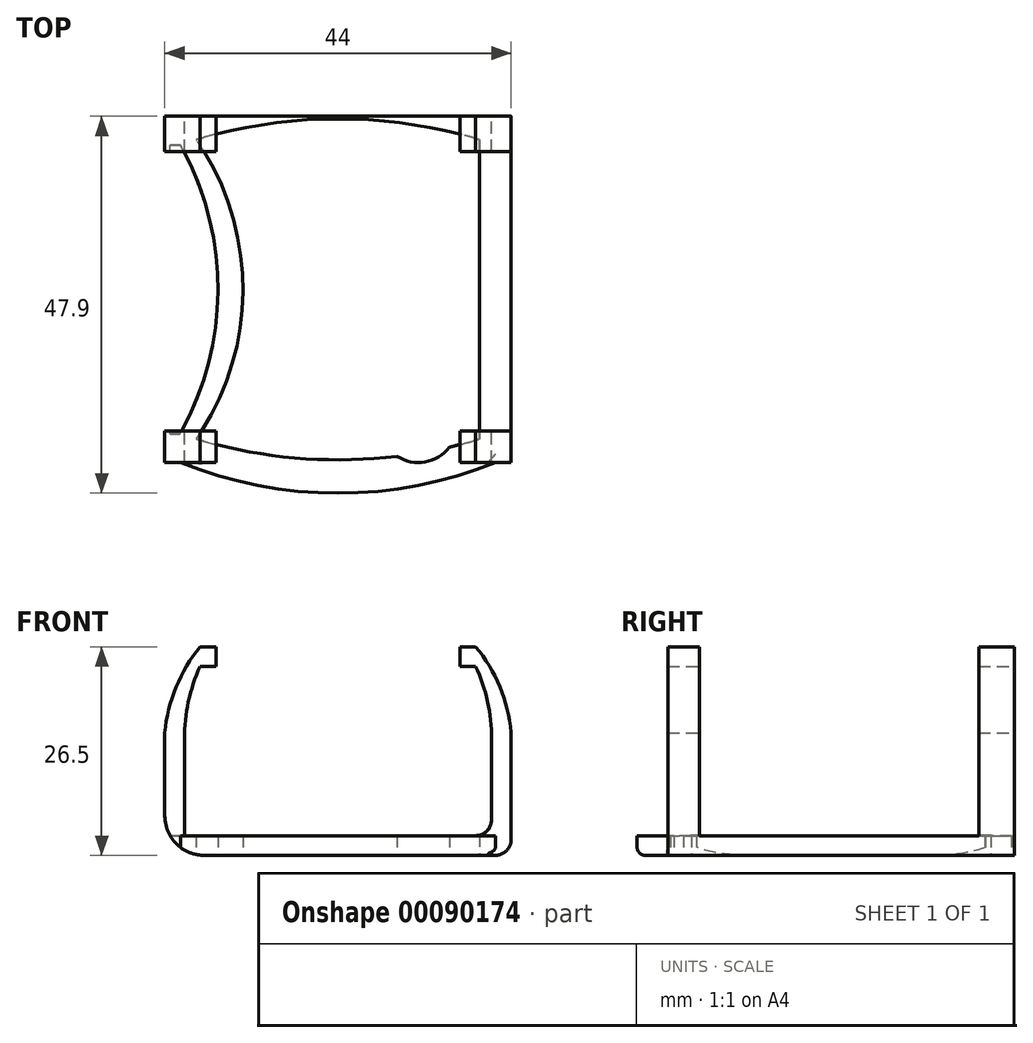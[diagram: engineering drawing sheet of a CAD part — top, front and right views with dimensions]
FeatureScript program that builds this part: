
annotation { "Feature Type Name" : "Feature", "Feature Type Description" : "" }
export const myFeature = defineFeature(function(context is Context, id is Id, definition is map)
    precondition{}
    {
        {
            var Q0;
            Q0=qCreatedBy(makeId("Front.planeOp"),FACE);
            var sketch = newSketch(context, id + "F0", { "sketchPlane" : qUnion([Q0])});
            skLineSegment(sketch, "E0", {"start": v(0, 0) * mm, "end": v(19.5, 0) * mm});
            skLineSegment(sketch, "E1", {"start": v(19.5, 0) * mm, "end": v(19.5, 12.3) * mm});
            skLineSegment(sketch, "E2", {"start": v(22, 13.05) * mm, "end": v(22, -2.5) * mm});
            skLineSegment(sketch, "E3", {"start": v(22, -2.5) * mm, "end": v(0, -2.5) * mm});
            skArc(sketch, "E4", {"start": v(19.5, 12.3) * mm, "mid": v(19.01, 17.02) * mm, "end": v(17.5, 21.5) * mm});
            skArc(sketch, "E5", {"start": v(22, 13.05) * mm, "mid": v(20.57, 18.86) * mm, "end": v(17.5, 24) * mm});
            skLineSegment(sketch, "E6", {"start": v(17.5, 21.5) * mm, "end": v(15.5, 21.5) * mm});
            skLineSegment(sketch, "E7", {"start": v(15.5, 21.5) * mm, "end": v(15.5, 24) * mm});
            skLineSegment(sketch, "E8", {"start": v(15.5, 24) * mm, "end": v(17.5, 24) * mm});
            skLineSegment(sketch, "E9.MirrorCS", {"start": v(-17.5, 21.5) * mm, "end": v(-15.5, 21.5) * mm});
            skArc(sketch, "E10.MirrorCS", {"start": v(-19.5, 12.3) * mm, "mid": v(-19.01, 17.02) * mm, "end": v(-17.5, 21.5) * mm});
            skLineSegment(sketch, "E11.MirrorCS", {"start": v(-22, 13.05) * mm, "end": v(-22, -2.5) * mm});
            skLineSegment(sketch, "E12.MirrorCS", {"start": v(-19.5, 0) * mm, "end": v(-19.5, 12.3) * mm});
            skArc(sketch, "E13.MirrorCS", {"start": v(-22, 13.05) * mm, "mid": v(-20.57, 18.86) * mm, "end": v(-17.5, 24) * mm});
            skLineSegment(sketch, "E14.MirrorCS", {"start": v(-15.5, 24) * mm, "end": v(-17.5, 24) * mm});
            skLineSegment(sketch, "E15.MirrorCS", {"start": v(-22, -2.5) * mm, "end": v(0, -2.5) * mm});
            skLineSegment(sketch, "E16.MirrorCS", {"start": v(0, 0) * mm, "end": v(-19.5, 0) * mm});
            skLineSegment(sketch, "E17.MirrorCS", {"start": v(-15.5, 21.5) * mm, "end": v(-15.5, 24) * mm});
            skSolve(sketch);
        }
        {
            var Q0;
            Q0=makeQuery(id+"F0.imprint","IMPRINT",FACE,{"disambiguationData":[TD([[makeQuery(id+"F0.imprint","IMPRINT",EDGE,{"derivedFrom":sQuery(id+"F0.wireOp",EDGE,"E0")}),-1.0]])]});
            extrude(context, id + "F1", {"entities" : qUnion([Q0]), "depth" : 44 * mm});
        }
        {
            var Q0;
            Q0=makeQuery(id+"F1.opExtrude","SWEPT_FACE",FACE,{"disambiguationData":[OSD([sQuery(id+"F0.wireOp",EDGE,"E2")])]});
            var sketch = newSketch(context, id + "F2", { "sketchPlane" : qUnion([Q0])});
            skLineSegment(sketch, "E18", {"start": v(-40, 13.05) * mm, "end": v(-40, 0) * mm});
            skLineSegment(sketch, "E19", {"start": v(-40, 0) * mm, "end": v(-4.5, 0) * mm});
            skLineSegment(sketch, "E20", {"start": v(-4.5, 0) * mm, "end": v(-4.5, 13.05) * mm});
            skLineSegment(sketch, "E21", {"start": v(-4.5, 13.05) * mm, "end": v(-4.5, 24.05) * mm});
            skLineSegment(sketch, "E22", {"start": v(-4.5, 24.05) * mm, "end": v(-40, 24.05) * mm});
            skLineSegment(sketch, "E23", {"start": v(-40, 24.05) * mm, "end": v(-40, 13.05) * mm});
            skSolve(sketch);
        }
        {
            var Q0;
            Q0=makeQuery(id+"F1.opExtrude","SWEPT_EDGE",EDGE,{"disambiguationData":[OSD([sQuery(id+"F0.wireOp",EDGE,"ead0873c-5f46-45a2-a165-93b22b89707c5.MirrorCS"),sQuery(id+"F0.wireOp",EDGE,"ead0873c-5f46-45a2-a165-93b22b89707c6.MirrorCS")])]});
            var Q1;
            Q1=makeQuery(id+"F1.opExtrude","SWEPT_EDGE",EDGE,{"disambiguationData":[OSD([sQuery(id+"F0.wireOp",EDGE,"Wcccyxxx-FNSd-Qq9p-4Mge-pHL6YJXQHdxu"),sQuery(id+"F0.wireOp",EDGE,"E2")])]});
            var Q2;
            Q2=makeQuery(id+"F1.opExtrude","SWEPT_EDGE",EDGE,{"disambiguationData":[OSD([sQuery(id+"F0.wireOp",EDGE,"ead0873c-5f46-45a2-a165-93b22b89707c2.MirrorCS"),sQuery(id+"F0.wireOp",EDGE,"ead0873c-5f46-45a2-a165-93b22b89707c3.MirrorCS")])]});
            var Q3;
            Q3=makeQuery(id+"F1.opExtrude","SWEPT_EDGE",EDGE,{"disambiguationData":[OSD([sQuery(id+"F0.wireOp",EDGE,"E0"),sQuery(id+"F0.wireOp",EDGE,"E1")])]});
            var Q4;
            Q4=makeQuery(id+"F1.opExtrude","SWEPT_EDGE",EDGE,{"disambiguationData":[OSD([sQuery(id+"F0.wireOp",EDGE,"ead0873c-5f46-45a2-a165-93b22b89707c4.MirrorCS"),sQuery(id+"F0.wireOp",EDGE,"ead0873c-5f46-45a2-a165-93b22b89707c5.MirrorCS")])]});
            var Q5;
            Q5=makeQuery(id+"F1.opExtrude","SWEPT_EDGE",EDGE,{"disambiguationData":[OSD([sQuery(id+"F0.wireOp",EDGE,"E2"),sQuery(id+"F0.wireOp",EDGE,"E3")])]});
            fillet(context, id + "F3", {"entities" : qUnion([Q0, Q1, Q2, Q3, Q4, Q5]), "radius" : 2 * mm, "tangentPropagation" : true, "allowEdgeOverflow" : false});
        }
        {
            var Q0;
            Q0 = qSketchRegion(id + "F2", true);
            extrude(context, id + "F4", {"entities" : qUnion([Q0]), "operationType" : NewBodyOperationType.REMOVE, "endBound" : BoundingType.THROUGH_ALL, "oppositeDirection" : true, "depth" : 25 * mm});
        }
        {
            var Q0;
            Q0=makeQuery(id+"F1.opExtrude","SWEPT_FACE",FACE,{"disambiguationData":[OSD([sQuery(id+"F0.wireOp",EDGE,"E3"),sQuery(id+"F0.wireOp",EDGE,"ead0873c-5f46-45a2-a165-93b22b89707c4.MirrorCS")])]});
            var sketch = newSketch(context, id + "F5", { "sketchPlane" : qUnion([Q0])});
            skArc(sketch, "E24", {"start": v(20, 44) * mm, "mid": v(0, 47.9) * mm, "end": v(-20, 44) * mm});
            skArc(sketch, "E25", {"start": v(14.17, 42.04) * mm, "mid": v(11.06, 43.92) * mm, "end": v(7.5, 43.2) * mm});
            skLineSegment(sketch, "E26", {"start": v(-25.94, 40.39) * mm, "end": v(33.24, 40.39) * mm, "construction": true});
            skArc(sketch, "E27", {"start": v(18, 41.02) * mm, "mid": v(16.1, 41.56) * mm, "end": v(14.17, 42.04) * mm});
            skLineSegment(sketch, "E28", {"start": v(20, 22) * mm, "end": v(-23.8, 22) * mm, "construction": true});
            skArc(sketch, "E29.MirrorCS", {"start": v(18, 2.98) * mm, "mid": v(0, 0.34) * mm, "end": v(-18, 2.98) * mm});
            skArc(sketch, "E30.MirrorCS", {"start": v(20, 0) * mm, "mid": v(0, -3.9) * mm, "end": v(-20, 0) * mm});
            skArc(sketch, "E31.trimOffspring", {"start": v(7.5, 43.2) * mm, "mid": v(-5.36, 43.43) * mm, "end": v(-18, 41.02) * mm});
            skLineSegment(sketch, "E32", {"start": v(18, 47.5) * mm, "end": v(18, 44.76) * mm});
            skLineSegment(sketch, "E33.MirrorCS", {"start": v(-18, 41.02) * mm, "end": v(-18, 40.39) * mm});
            skPoint(sketch, "E34.orphan", {"position": v(-18, 47.5) * mm});
            skPoint(sketch, "E35.orphan", {"position": v(-20, 40.39) * mm});
            skPoint(sketch, "E36.orphan", {"position": v(-20, 3.61) * mm});
            skPoint(sketch, "E37.orphan", {"position": v(-18, -5.06) * mm});
            skPoint(sketch, "E38.trimOffspring.end.orphan", {"position": v(18, -5.06) * mm});
            skPoint(sketch, "E39.orphan", {"position": v(20, 3.61) * mm});
            skPoint(sketch, "E40.orphan", {"position": v(20, 40.39) * mm});
            skLineSegment(sketch, "E41.trimOffspring", {"start": v(18, 41.02) * mm, "end": v(18, 2.98) * mm});
            skLineSegment(sketch, "E42", {"start": v(-20, 44) * mm, "end": v(-20, 40.39) * mm});
            skLineSegment(sketch, "E43", {"start": v(20, 44) * mm, "end": v(20, 0) * mm});
            skArc(sketch, "E44", {"start": v(-18, 2.98) * mm, "mid": v(-12.07, 22) * mm, "end": v(-18, 41.02) * mm});
            skArc(sketch, "E45", {"start": v(-20, 3.61) * mm, "mid": v(-15.24, 22) * mm, "end": v(-20, 40.39) * mm});
            skLineSegment(sketch, "E46.trimOffspring", {"start": v(-20, 3.61) * mm, "end": v(-20, 0) * mm});
            skSolve(sketch);
        }
        {
            var Q0;
            {var subQ5=sQuery(id+"F5.wireOp",EDGE,"E27");Q0=makeQuery(id+"F5.imprint","IMPRINT",FACE,{"disambiguationData":[TD([[makeQuery(id+"F5.imprint","IMPRINT",EDGE,{"derivedFrom":subQ5}),-1.0]])]});}
            var Q1;
            Q1=makeQuery(id+"F5.imprint","IMPRINT",FACE,{"disambiguationData":[TD([[makeQuery(id+"F5.imprint","IMPRINT",EDGE,{"derivedFrom":sQuery(id+"F5.wireOp",EDGE,"E30.MirrorCS")}),-1.0]])]});
            var Q2;
            {var subQ0=sQuery(id+"F5.wireOp",EDGE,"E24");var subQ3=makeQuery(id+"F5.imprint","IMPRINT",VERTEX,{"derivedFrom":subQ0});Q2=makeQuery(id+"F5.imprint","IMPRINT",FACE,{"disambiguationData":[TD([[makeQuery(id+"F5.imprint","IMPRINT",EDGE,{"disambiguationData":[TD([[subQ3,1.0]])],"derivedFrom":subQ0}),1.0]])]});}
            extrude(context, id + "F6", {"entities" : qUnion([Q0, Q1, Q2]), "operationType" : NewBodyOperationType.ADD, "oppositeDirection" : true, "depth" : 2.5 * mm});
        }
        {
            var Q0;
            {var subQ3=sQuery(id+"F5.wireOp",EDGE,"E27");Q0=makeQuery(id+"F5.imprint","IMPRINT",FACE,{"disambiguationData":[TD([[makeQuery(id+"F5.imprint","IMPRINT",EDGE,{"derivedFrom":subQ3}),1.0]])]});}
            extrude(context, id + "F7", {"entities" : qUnion([Q0]), "operationType" : NewBodyOperationType.REMOVE, "oppositeDirection" : true, "depth" : 15.75 * mm});
        }
        {
            var Q0;
            Q0=makeQuery(id+"F7.boolean.opBoolean","COPY",EDGE,{"derivedFrom":makeQuery(id+"F7.opExtrude","CAP_EDGE",EDGE,{"disambiguationData":[OSD([sQuery(id+"F5.wireOp",EDGE,"E31.trimOffspring")])],"isStart":true})});
            var Q1;
            Q1=makeQuery(id+"F7.boolean.opBoolean","COPY",EDGE,{"derivedFrom":makeQuery(id+"F7.opExtrude","CAP_EDGE",EDGE,{"disambiguationData":[OSD([sQuery(id+"F5.wireOp",EDGE,"E33.MirrorCS")])],"isStart":true})});
            var Q2;
            Q2=makeQuery(id+"F7.boolean.opBoolean","COPY",EDGE,{"derivedFrom":makeQuery(id+"F7.opExtrude","CAP_EDGE",EDGE,{"disambiguationData":[OSD([sQuery(id+"F5.wireOp",EDGE,"E29.MirrorCS")])],"isStart":true})});
            var Q3;
            Q3=makeQuery(id+"F7.boolean.opBoolean","COPY",EDGE,{"derivedFrom":makeQuery(id+"F7.opExtrude","CAP_EDGE",EDGE,{"disambiguationData":[OSD([sQuery(id+"F5.wireOp",EDGE,"E41.trimOffspring")])],"isStart":true})});
            var Q4;
            Q4=makeQuery(id+"F7.boolean.opBoolean","COPY",EDGE,{"derivedFrom":makeQuery(id+"F7.opExtrude","CAP_EDGE",EDGE,{"disambiguationData":[OSD([sQuery(id+"F5.wireOp",EDGE,"E27")])],"isStart":true})});
            var Q5;
            Q5=makeQuery(id+"F7.boolean.opBoolean","COPY",EDGE,{"derivedFrom":makeQuery(id+"F7.opExtrude","CAP_EDGE",EDGE,{"disambiguationData":[OSD([sQuery(id+"F5.wireOp",EDGE,"E25")])],"isStart":true})});
            var Q6;
            Q6=makeQuery(id+"F6.opExtrude","CAP_EDGE",EDGE,{"disambiguationData":[OSD([sQuery(id+"F5.wireOp",EDGE,"E24")])],"isStart":true});
            var Q7;
            Q7=makeQuery(id+"F6.opExtrude","CAP_EDGE",EDGE,{"disambiguationData":[OSD([sQuery(id+"F5.wireOp",EDGE,"E30.MirrorCS")])],"isStart":true});
            fillet(context, id + "F8", {"entities" : qUnion([Q0, Q1, Q2, Q3, Q4, Q5, Q6, Q7]), "radius" : 1 * mm, "tangentPropagation" : true, "allowEdgeOverflow" : false});
        }
        {
            var Q0;
            {var subQ4=sQuery(id+"F5.wireOp",EDGE,"E42");Q0=makeQuery(id+"F5.imprint","IMPRINT",FACE,{"disambiguationData":[TD([[makeQuery(id+"F5.imprint","IMPRINT",EDGE,{"derivedFrom":subQ4}),-1.0]])]});}
            var sketch = newSketch(context, id + "F9", { "sketchPlane" : qUnion([Q0])});
            skArc(sketch, "E47", {"start": v(-20.01, 3.69) * mm, "mid": v(-15.24, 22.04) * mm, "end": v(-20.07, 40.37) * mm});
            skLineSegment(sketch, "E48", {"start": v(-20.07, 40.37) * mm, "end": v(-22.72, 40.37) * mm});
            skLineSegment(sketch, "E49", {"start": v(-22.72, 40.37) * mm, "end": v(-22.72, 3.69) * mm});
            skLineSegment(sketch, "E50", {"start": v(-22.72, 3.69) * mm, "end": v(-20.01, 3.69) * mm});
            skSolve(sketch);
        }
        {
            var Q0;
            Q0 = qSketchRegion(id + "F9", true);
            var Q1;
            {var subQ0=sQuery(id+"F5.wireOp",EDGE,"E24");var subQ1=sQuery(id+"F5.wireOp",EDGE,"E30.MirrorCS");var subQ3=sQuery(id+"F0.wireOp",EDGE,"E0");var subQ5=sQuery(id+"F0.wireOp",EDGE,"E16.MirrorCS");var subQ10=sQuery(id+"F0.wireOp",EDGE,"E11.MirrorCS");var subQ20=sQuery(id+"F5.wireOp",EDGE,"E31.trimOffspring");var subQ21=sQuery(id+"F5.wireOp",EDGE,"E25");var subQ22=sQuery(id+"F5.wireOp",EDGE,"E27");var subQ23=sQuery(id+"F5.wireOp",EDGE,"E29.MirrorCS");var subQ24=sQuery(id+"F5.wireOp",EDGE,"E44");Q1=makeQuery(id+"F7.boolean.opBoolean","SPLIT",FACE,{"disambiguationData":[TD([makeQuery(id+"F1.opExtrude","SWEPT_FACE",FACE,{"disambiguationData":[OSD([subQ10])]})])],"derivedFrom":makeQuery(id+"F6.boolean.opBoolean","MERGE",FACE,{"derivedFrom":[makeQuery(id+"F4.boolean.opBoolean","MERGE",FACE,{"derivedFrom":[makeQuery(id+"F1.opExtrude","SWEPT_FACE",FACE,{"disambiguationData":[OSD([subQ3,subQ5])]}),makeQuery(id+"F4.opExtrude","SWEPT_FACE",FACE,{"disambiguationData":[OSD([sQuery(id+"F2.wireOp",EDGE,"E19")])]})]}),makeQuery(id+"F6.opExtrude","CAP_FACE",FACE,{"disambiguationData":[OSD([subQ0,subQ21,subQ22,subQ23,subQ1,subQ20,sQuery(id+"F5.wireOp",EDGE,"E41.trimOffspring"),sQuery(id+"F5.wireOp",EDGE,"E42"),sQuery(id+"F5.wireOp",EDGE,"E43"),subQ24,sQuery(id+"F5.wireOp",EDGE,"E45"),sQuery(id+"F5.wireOp",EDGE,"E46.trimOffspring")])],"isStart":false})]})});}
            extrude(context, id + "F10", {"entities" : qUnion([Q0]), "operationType" : NewBodyOperationType.REMOVE, "endBound" : BoundingType.UP_TO_SURFACE, "oppositeDirection" : true, "endBoundEntityFace" : qUnion([Q1]), "depth" : 25 * mm});
        }
        {
            var Q0;
            {var subQ0=sQuery(id+"F0.wireOp",EDGE,"E15.MirrorCS");var subQ2=sQuery(id+"F0.wireOp",EDGE,"E11.MirrorCS");Q0=makeQuery(id+"F10.boolean.opBoolean","SPLIT",EDGE,{"disambiguationData":[TD([makeQuery(id+"F10.opExtrude","SWEPT_FACE",FACE,{"disambiguationData":[OSD([sQuery(id+"F9.wireOp",EDGE,"E48")])]})])],"derivedFrom":makeQuery(id+"F1.opExtrude","SWEPT_EDGE",EDGE,{"disambiguationData":[OSD([subQ2,subQ0])]})});}
            var Q1;
            {var subQ0=sQuery(id+"F0.wireOp",EDGE,"E15.MirrorCS");var subQ2=sQuery(id+"F0.wireOp",EDGE,"E11.MirrorCS");Q1=makeQuery(id+"F10.boolean.opBoolean","SPLIT",EDGE,{"disambiguationData":[TD([makeQuery(id+"F10.opExtrude","SWEPT_FACE",FACE,{"disambiguationData":[OSD([sQuery(id+"F9.wireOp",EDGE,"E50")])]})])],"derivedFrom":makeQuery(id+"F1.opExtrude","SWEPT_EDGE",EDGE,{"disambiguationData":[OSD([subQ2,subQ0])]})});}
            fillet(context, id + "F11", {"entities" : qUnion([Q0, Q1]), "radius" : 5 * mm, "tangentPropagation" : true, "allowEdgeOverflow" : false});
        }
    });
